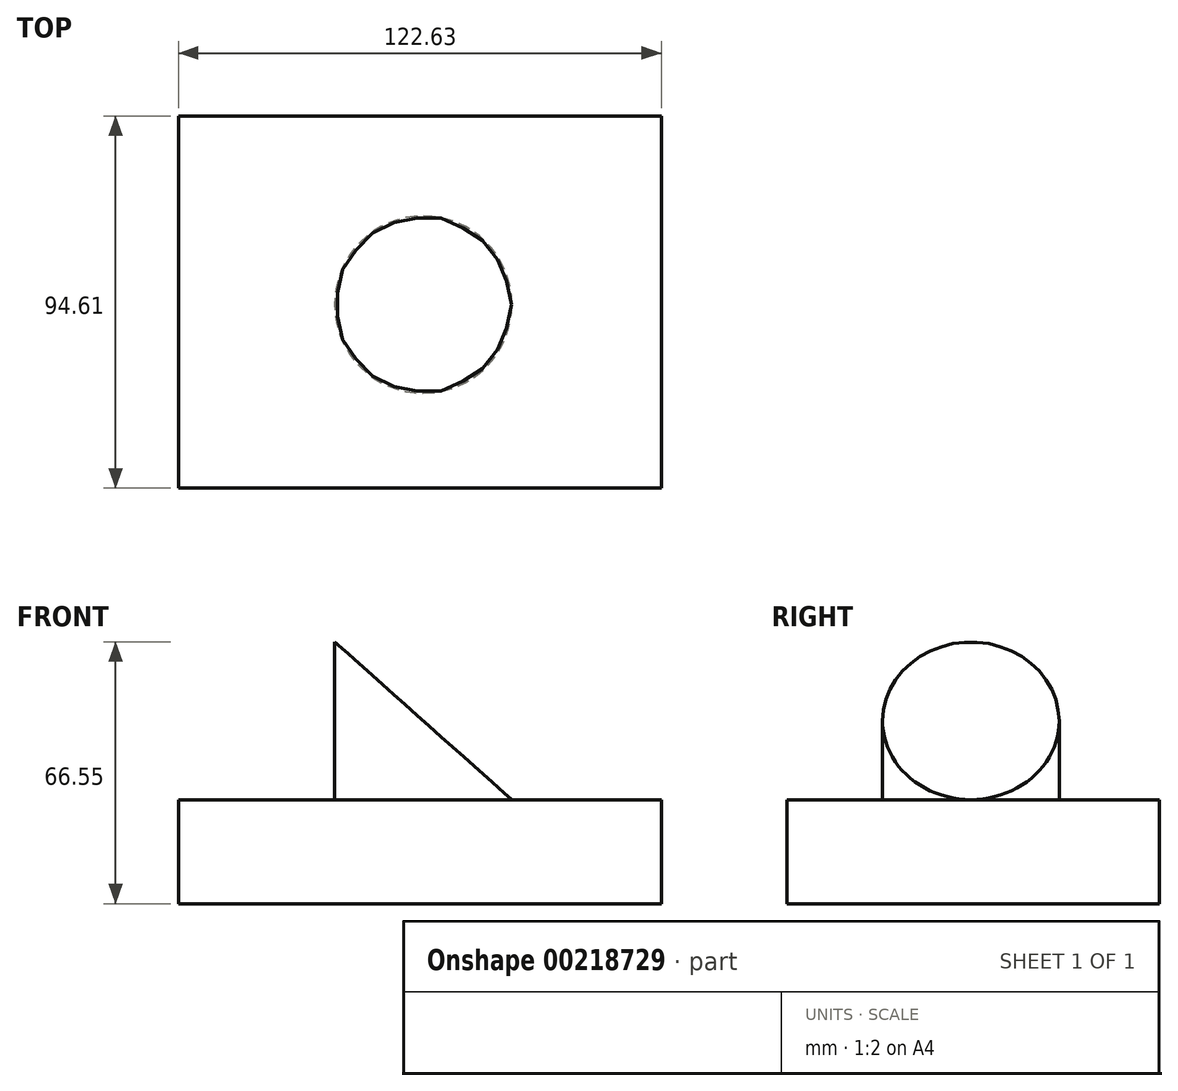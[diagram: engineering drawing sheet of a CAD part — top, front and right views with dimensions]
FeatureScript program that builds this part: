
annotation { "Feature Type Name" : "Feature", "Feature Type Description" : "" }
export const myFeature = defineFeature(function(context is Context, id is Id, definition is map)
    precondition{}
    {
        {
            var Q0;
            Q0=qCreatedBy(makeId("Top.planeOp"),FACE);
            var sketch = newSketch(context, id + "F0", { "sketchPlane" : qUnion([Q0])});
            skLineSegment(sketch, "E0.bottom", {"start": v(-62.15, 47.96) * mm, "end": v(60.48, 47.96) * mm});
            skLineSegment(sketch, "E0.top", {"start": v(-62.15, -46.65) * mm, "end": v(60.48, -46.65) * mm});
            skLineSegment(sketch, "E0.left", {"start": v(-62.15, 47.96) * mm, "end": v(-62.15, -46.65) * mm});
            skLineSegment(sketch, "E0.right", {"start": v(60.48, 47.96) * mm, "end": v(60.48, -46.65) * mm});
            skSolve(sketch);
        }
        {
            var Q0;
            Q0 = qSketchRegion(id + "F0", true);
            extrude(context, id + "F1", {"entities" : qUnion([Q0]), "depth" : 26.42 * mm});
        }
        {
            var Q0;
            Q0=makeQuery(id+"F1.opExtrude","CAP_FACE",FACE,{"disambiguationData":[OSD([sQuery(id+"F0.wireOp",EDGE,"E0.bottom"),sQuery(id+"F0.wireOp",EDGE,"E0.top"),sQuery(id+"F0.wireOp",EDGE,"E0.left"),sQuery(id+"F0.wireOp",EDGE,"E0.right")])],"isStart":false});
            var sketch = newSketch(context, id + "F2", { "sketchPlane" : qUnion([Q0])});
            skCircle(sketch, "E1", {"center": v(0, 0) * mm, "radius": 22.5 * mm});
            skSolve(sketch);
        }
        {
            var Q0;
            Q0 = qSketchRegion(id + "F2", true);
            extrude(context, id + "F3", {"entities" : qUnion([Q0]), "depth" : 40.13 * mm});
        }
        {
            var Q0;
            Q0=makeQuery(id+"F1.opExtrude","SWEPT_FACE",FACE,{"disambiguationData":[OSD([sQuery(id+"F0.wireOp",EDGE,"E0.top")])]});
            var sketch = newSketch(context, id + "F4", { "sketchPlane" : qUnion([Q0])});
            skLineSegment(sketch, "E2", {"start": v(-22.5, 26.42) * mm, "end": v(-22.5, 66.55) * mm});
            skLineSegment(sketch, "E3", {"start": v(22.5, 66.55) * mm, "end": v(22.5, 26.42) * mm});
            skLineSegment(sketch, "E4", {"start": v(-22.5, 66.55) * mm, "end": v(22.5, 26.42) * mm});
            skLineSegment(sketch, "E5", {"start": v(22.5, 66.55) * mm, "end": v(-22.5, 66.55) * mm});
            skSolve(sketch);
        }
        {
            var Q0;
            Q0=makeQuery(id+"F4.imprint","IMPRINT",FACE,{"disambiguationData":[TD([[makeQuery(id+"F4.imprint","IMPRINT",EDGE,{"derivedFrom":sQuery(id+"F4.wireOp",EDGE,"E4")}),1.0]])]});
            extrude(context, id + "F5", {"entities" : qUnion([Q0]), "operationType" : NewBodyOperationType.REMOVE, "endBound" : BoundingType.THROUGH_ALL, "oppositeDirection" : true, "depth" : 25.4 * mm});
        }
    });
